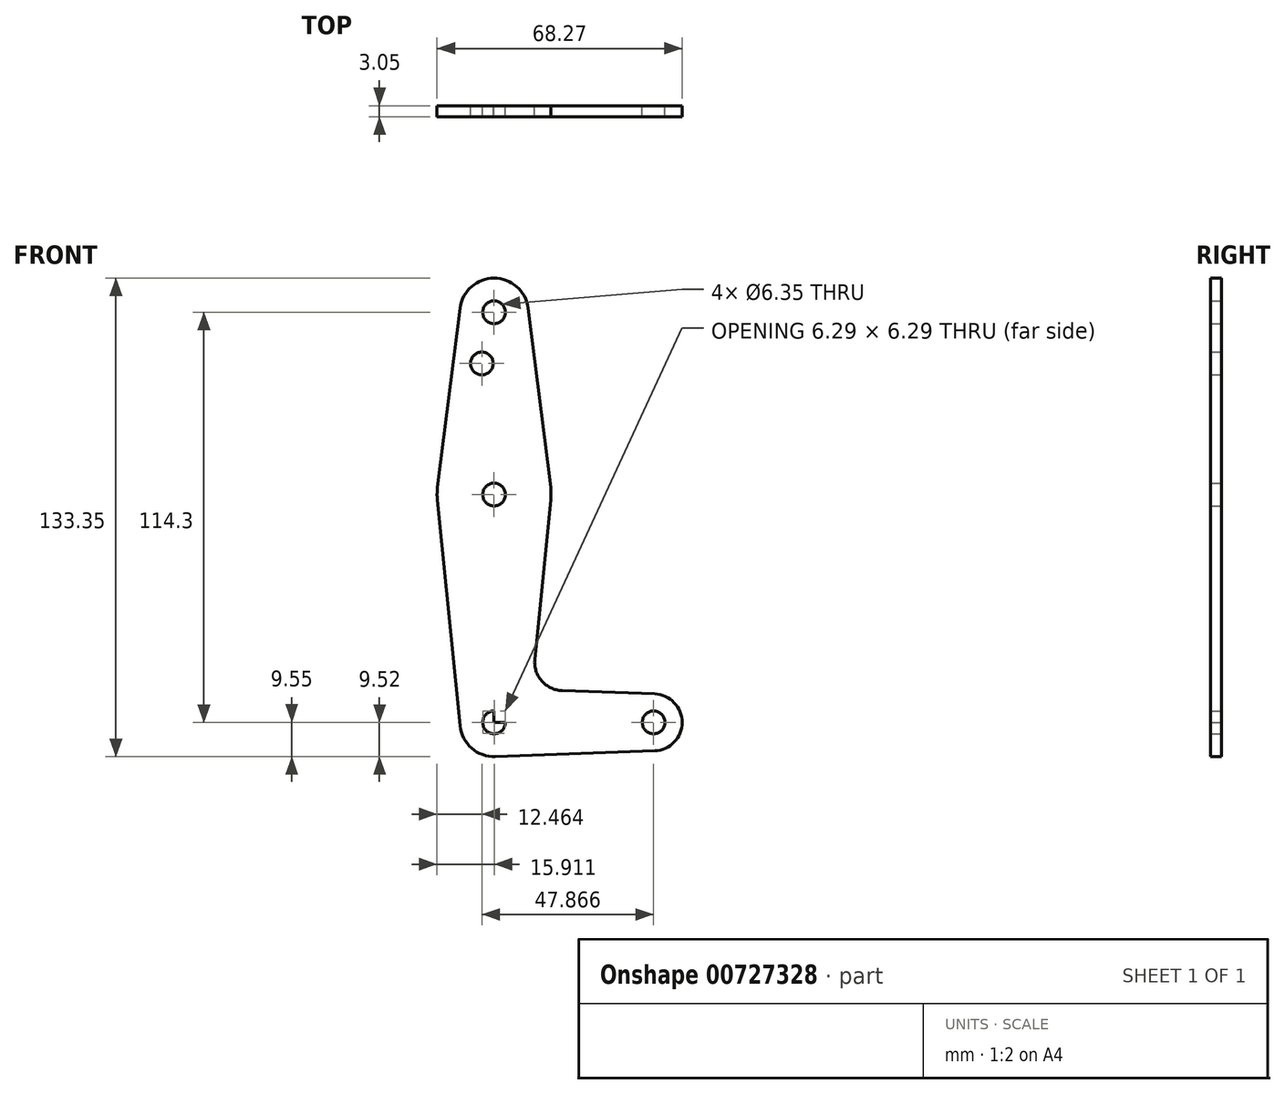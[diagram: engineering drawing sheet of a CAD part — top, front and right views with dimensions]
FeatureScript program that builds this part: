
annotation { "Feature Type Name" : "Feature", "Feature Type Description" : "" }
export const myFeature = defineFeature(function(context is Context, id is Id, definition is map)
    precondition{}
    {
        {
            var Q0;
            Q0=qCreatedBy(makeId("Front.planeOp"),FACE);
            var sketch = newSketch(context, id + "F0", { "sketchPlane" : qUnion([Q0])});
            skLineSegment(sketch, "E0", {"start": v(0, 0) * mm, "end": v(0, 63.5) * mm});
            skLineSegment(sketch, "E1", {"start": v(0, 0) * mm, "end": v(44.45, 0) * mm});
            skArc(sketch, "E2", {"start": v(9.45, 115.5) * mm, "mid": v(0, 123.83) * mm, "end": v(-9.45, 115.5) * mm});
            skArc(sketch, "E3", {"start": v(-9.48, -0.95) * mm, "mid": v(-6.26, -7.18) * mm, "end": v(0.34, -9.52) * mm});
            skArc(sketch, "E4", {"start": v(44.73, -7.93) * mm, "mid": v(52.39, 0) * mm, "end": v(44.73, 7.93) * mm});
            skArc(sketch, "E5", {"start": v(-15.75, 65.48) * mm, "mid": v(-15.87, 63.7) * mm, "end": v(-15.8, 61.91) * mm});
            skLineSegment(sketch, "E6", {"start": v(9.45, 115.5) * mm, "end": v(15.75, 65.48) * mm});
            skLineSegment(sketch, "E7", {"start": v(-9.45, 115.5) * mm, "end": v(-15.75, 65.48) * mm});
            skLineSegment(sketch, "E8", {"start": v(15.8, 61.91) * mm, "end": v(11.34, 17.6) * mm});
            skLineSegment(sketch, "E9", {"start": v(-9.48, -0.95) * mm, "end": v(-15.8, 61.91) * mm});
            skLineSegment(sketch, "E10", {"start": v(18.97, 8.85) * mm, "end": v(44.73, 7.93) * mm});
            skLineSegment(sketch, "E11", {"start": v(0.34, -9.52) * mm, "end": v(44.73, -7.93) * mm});
            skCircle(sketch, "E12", {"center": v(0, 114.3) * mm, "radius": 3.18 * mm});
            skCircle(sketch, "E13", {"center": v(0, 63.5) * mm, "radius": 3.18 * mm});
            skCircle(sketch, "E14", {"center": v(0, 0) * mm, "radius": 3.18 * mm});
            skCircle(sketch, "E15", {"center": v(44.45, 0) * mm, "radius": 3.18 * mm});
            skCircle(sketch, "E16", {"center": v(-3.42, 100.03) * mm, "radius": 3.18 * mm});
            skPoint(sketch, "E17.newPointB", {"position": v(0.34, 9.52) * mm});
            skArc(sketch, "E17.filletArc", {"start": v(11.34, 17.6) * mm, "mid": v(13.26, 11.57) * mm, "end": v(18.97, 8.85) * mm});
            skArc(sketch, "E18.trimOffspring", {"start": v(15.8, 61.91) * mm, "mid": v(15.87, 63.7) * mm, "end": v(15.75, 65.48) * mm});
            skArc(sketch, "E19.trimOffspring", {"start": v(0.34, 9.52) * mm, "mid": v(0.17, 9.52) * mm, "end": v(0, 9.52) * mm});
            skSolve(sketch);
        }
        {
            var Q0;
            Q0 = qSketchRegion(id + "F0", true);
            var Q1;
            {var subQ0=sQuery(id+"F0.wireOp",EDGE,"E14");var subQ1=sQuery(id+"F0.wireOp",EDGE,"E0");var subQ2=makeQuery(id+"F0.imprint","INTERSECT",VERTEX,{"derivedFrom":[subQ1,subQ0]});Q1=makeQuery(id+"F0.imprint","IMPRINT",FACE,{"disambiguationData":[TD([[makeQuery(id+"F0.imprint","IMPRINT",EDGE,{"disambiguationData":[TD([[subQ2,-1.0]])],"derivedFrom":subQ1}),-1.0]])]});}
            extrude(context, id + "F1", {"entities" : qUnion([Q0, Q1]), "depth" : 3.05 * mm, "offsetDistance" : 25.4 * mm});
        }
    });
